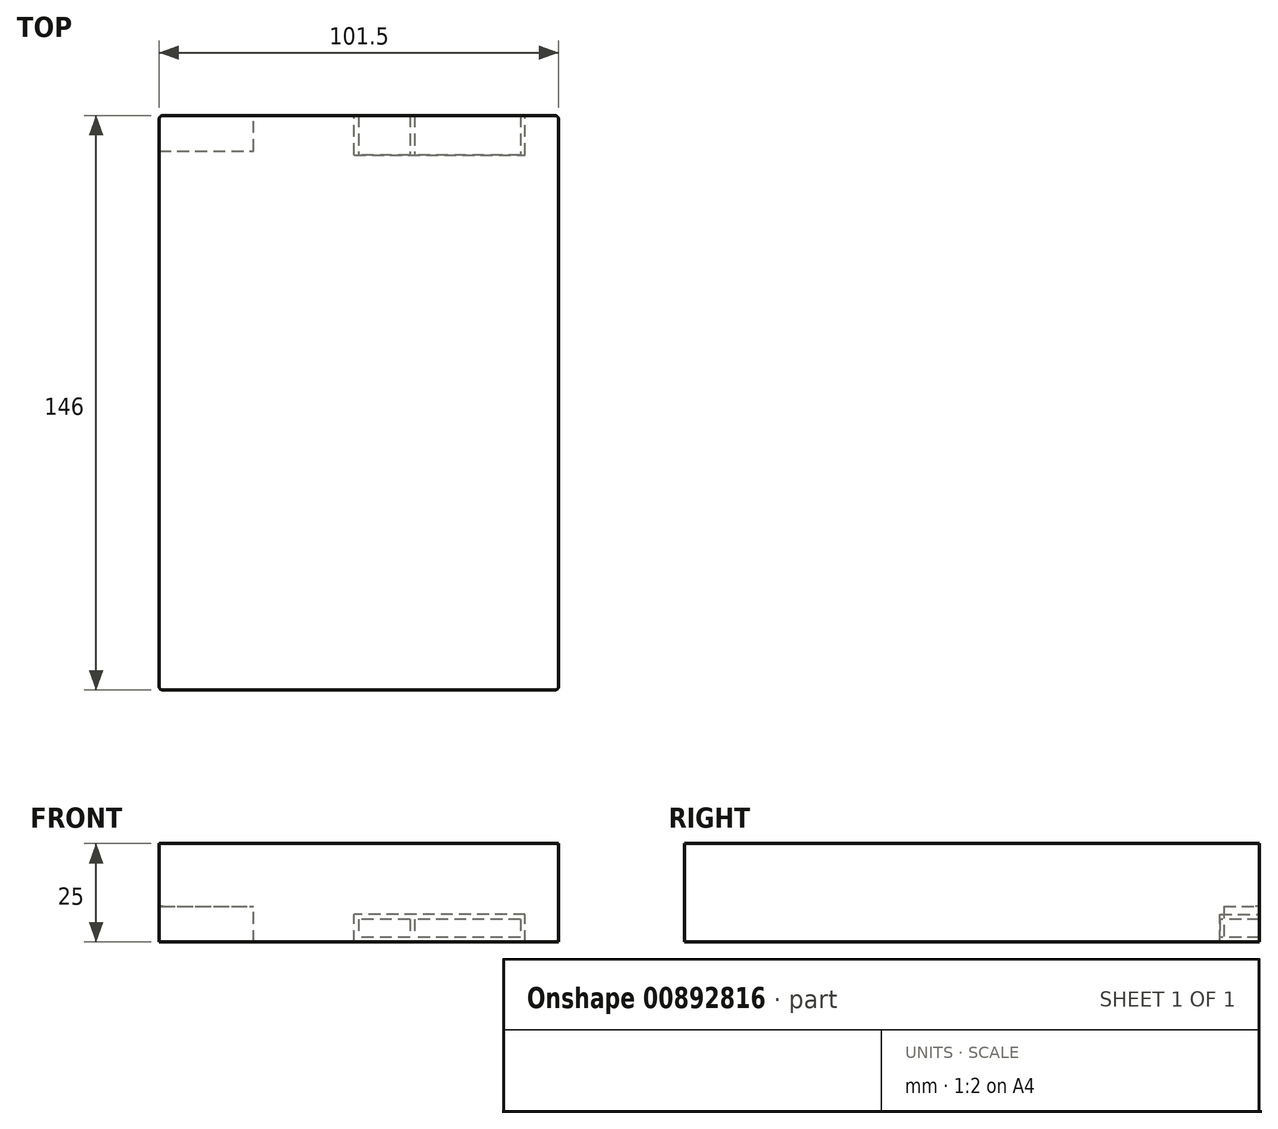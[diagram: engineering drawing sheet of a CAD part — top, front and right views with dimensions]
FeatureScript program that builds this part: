
annotation { "Feature Type Name" : "Feature", "Feature Type Description" : "" }
export const myFeature = defineFeature(function(context is Context, id is Id, definition is map)
    precondition{}
    {
        {
            var Q0;
            Q0=qCreatedBy(makeId("Top.planeOp"),FACE);
            var sketch = newSketch(context, id + "F0", { "sketchPlane" : qUnion([Q0])});
            skLineSegment(sketch, "E0.bottom", {"start": v(-50.75, 73) * mm, "end": v(50.75, 73) * mm});
            skLineSegment(sketch, "E0.top", {"start": v(-50.75, -73) * mm, "end": v(50.75, -73) * mm});
            skLineSegment(sketch, "E0.left", {"start": v(-50.75, 73) * mm, "end": v(-50.75, -73) * mm});
            skLineSegment(sketch, "E0.right", {"start": v(50.75, 73) * mm, "end": v(50.75, -73) * mm});
            skPoint(sketch, "E0.middle", {"position": v(0, 0) * mm});
            skSolve(sketch);
        }
        {
            var Q0;
            Q0=makeQuery(id+"F0.imprint","IMPRINT",FACE,{"disambiguationData":[TD([[makeQuery(id+"F0.imprint","IMPRINT",EDGE,{"derivedFrom":sQuery(id+"F0.wireOp",EDGE,"E0.bottom")}),-1.0]])]});
            extrude(context, id + "F1", {"entities" : qUnion([Q0]), "depth" : 25 * mm, "offsetDistance" : 25 * mm});
        }
        {
            var Q0;
            Q0=makeQuery(id+"F1.opExtrude","SWEPT_FACE",FACE,{"disambiguationData":[OSD([sQuery(id+"F0.wireOp",EDGE,"E0.bottom")])]});
            var sketch = newSketch(context, id + "F2", { "sketchPlane" : qUnion([Q0])});
            skLineSegment(sketch, "E1.bottom", {"start": v(50.75, 0) * mm, "end": v(26.75, 0) * mm});
            skLineSegment(sketch, "E1.top", {"start": v(50.75, 9) * mm, "end": v(26.75, 9) * mm});
            skLineSegment(sketch, "E1.left", {"start": v(50.75, 0) * mm, "end": v(50.75, 9) * mm});
            skLineSegment(sketch, "E1.right", {"start": v(26.75, 0) * mm, "end": v(26.75, 9) * mm});
            skSolve(sketch);
        }
        {
            var Q0;
            Q0=makeQuery(id+"F2.imprint","IMPRINT",FACE,{"disambiguationData":[TD([[makeQuery(id+"F2.imprint","IMPRINT",EDGE,{"derivedFrom":sQuery(id+"F2.wireOp",EDGE,"E1.bottom")}),-1.0]])]});
            extrude(context, id + "F3", {"entities" : qUnion([Q0]), "operationType" : NewBodyOperationType.REMOVE, "oppositeDirection" : true, "depth" : 9 * mm, "offsetDistance" : 25 * mm});
        }
        {
            var Q0;
            Q0=makeQuery(id+"F1.opExtrude","SWEPT_EDGE",EDGE,{"disambiguationData":[OSD([sQuery(id+"F0.wireOp",EDGE,"E0.bottom"),sQuery(id+"F0.wireOp",EDGE,"E0.right")])]});
            var Q1;
            Q1=makeQuery(id+"F1.opExtrude","SWEPT_EDGE",EDGE,{"disambiguationData":[OSD([sQuery(id+"F0.wireOp",EDGE,"E0.bottom"),sQuery(id+"F0.wireOp",EDGE,"E0.left")])]});
            var Q2;
            Q2=makeQuery(id+"F1.opExtrude","SWEPT_EDGE",EDGE,{"disambiguationData":[OSD([sQuery(id+"F0.wireOp",EDGE,"E0.top"),sQuery(id+"F0.wireOp",EDGE,"E0.left")])]});
            var Q3;
            Q3=makeQuery(id+"F1.opExtrude","SWEPT_EDGE",EDGE,{"disambiguationData":[OSD([sQuery(id+"F0.wireOp",EDGE,"E0.top"),sQuery(id+"F0.wireOp",EDGE,"E0.right")])]});
            fillet(context, id + "F4", {"entities" : qUnion([Q0, Q1, Q2, Q3]), "radius" : 1 * mm, "tangentPropagation" : true, "allowEdgeOverflow" : false});
        }
        {
            var Q0;
            Q0=makeQuery(id+"F1.opExtrude","SWEPT_FACE",FACE,{"disambiguationData":[OSD([sQuery(id+"F0.wireOp",EDGE,"E0.bottom")])]});
            var sketch = newSketch(context, id + "F5", { "sketchPlane" : qUnion([Q0])});
            skLineSegment(sketch, "E2.bottom", {"start": v(-42.25, 0) * mm, "end": v(1.25, 0) * mm});
            skLineSegment(sketch, "E2.top", {"start": v(-42.25, 7) * mm, "end": v(1.25, 7) * mm});
            skLineSegment(sketch, "E2.left", {"start": v(-42.25, 0) * mm, "end": v(-42.25, 7) * mm});
            skLineSegment(sketch, "E2.right", {"start": v(1.25, 0) * mm, "end": v(1.25, 7) * mm});
            skSolve(sketch);
        }
        {
            var Q0;
            Q0=makeQuery(id+"F5.imprint","IMPRINT",FACE,{"disambiguationData":[TD([[makeQuery(id+"F5.imprint","IMPRINT",EDGE,{"derivedFrom":sQuery(id+"F5.wireOp",EDGE,"E2.bottom")}),-1.0]])]});
            extrude(context, id + "F6", {"entities" : qUnion([Q0]), "operationType" : NewBodyOperationType.REMOVE, "oppositeDirection" : true, "depth" : 10 * mm, "offsetDistance" : 25 * mm});
        }
        {
            var Q0;
            Q0=makeQuery(id+"F6.boolean.opBoolean","COPY",FACE,{"derivedFrom":makeQuery(id+"F6.opExtrude","CAP_FACE",FACE,{"disambiguationData":[OSD([sQuery(id+"F5.wireOp",EDGE,"E2.bottom"),sQuery(id+"F5.wireOp",EDGE,"E2.top"),sQuery(id+"F5.wireOp",EDGE,"E2.left"),sQuery(id+"F5.wireOp",EDGE,"E2.right")])],"isStart":false})});
            var sketch = newSketch(context, id + "F7", { "sketchPlane" : qUnion([Q0])});
            skLineSegment(sketch, "E3.bottom", {"start": v(-41.05, 5.8) * mm, "end": v(-14.15, 5.8) * mm});
            skLineSegment(sketch, "E3.top", {"start": v(-41.05, 1.2) * mm, "end": v(-14.15, 1.2) * mm});
            skLineSegment(sketch, "E3.left", {"start": v(-41.05, 5.8) * mm, "end": v(-41.05, 1.2) * mm});
            skLineSegment(sketch, "E3.right", {"start": v(-14.15, 5.8) * mm, "end": v(-14.15, 1.2) * mm});
            skLineSegment(sketch, "E4.bottom", {"start": v(-12.95, 5.8) * mm, "end": v(0.05, 5.8) * mm});
            skLineSegment(sketch, "E4.top", {"start": v(-12.95, 1.2) * mm, "end": v(0.05, 1.2) * mm});
            skLineSegment(sketch, "E4.left", {"start": v(-12.95, 5.8) * mm, "end": v(-12.95, 1.2) * mm});
            skLineSegment(sketch, "E4.right", {"start": v(0.05, 5.8) * mm, "end": v(0.05, 1.2) * mm});
            skSolve(sketch);
        }
        {
            var Q0;
            Q0=makeQuery(id+"F7.imprint","IMPRINT",FACE,{"disambiguationData":[TD([[makeQuery(id+"F7.imprint","IMPRINT",EDGE,{"derivedFrom":sQuery(id+"F7.wireOp",EDGE,"E3.bottom")}),-1.0]])]});
            var Q1;
            Q1=makeQuery(id+"F7.imprint","IMPRINT",FACE,{"disambiguationData":[TD([[makeQuery(id+"F7.imprint","IMPRINT",EDGE,{"derivedFrom":sQuery(id+"F7.wireOp",EDGE,"E4.bottom")}),-1.0]])]});
            extrude(context, id + "F8", {"entities" : qUnion([Q0, Q1]), "operationType" : NewBodyOperationType.ADD, "depth" : 10 * mm, "offsetDistance" : 25 * mm});
        }
    });
